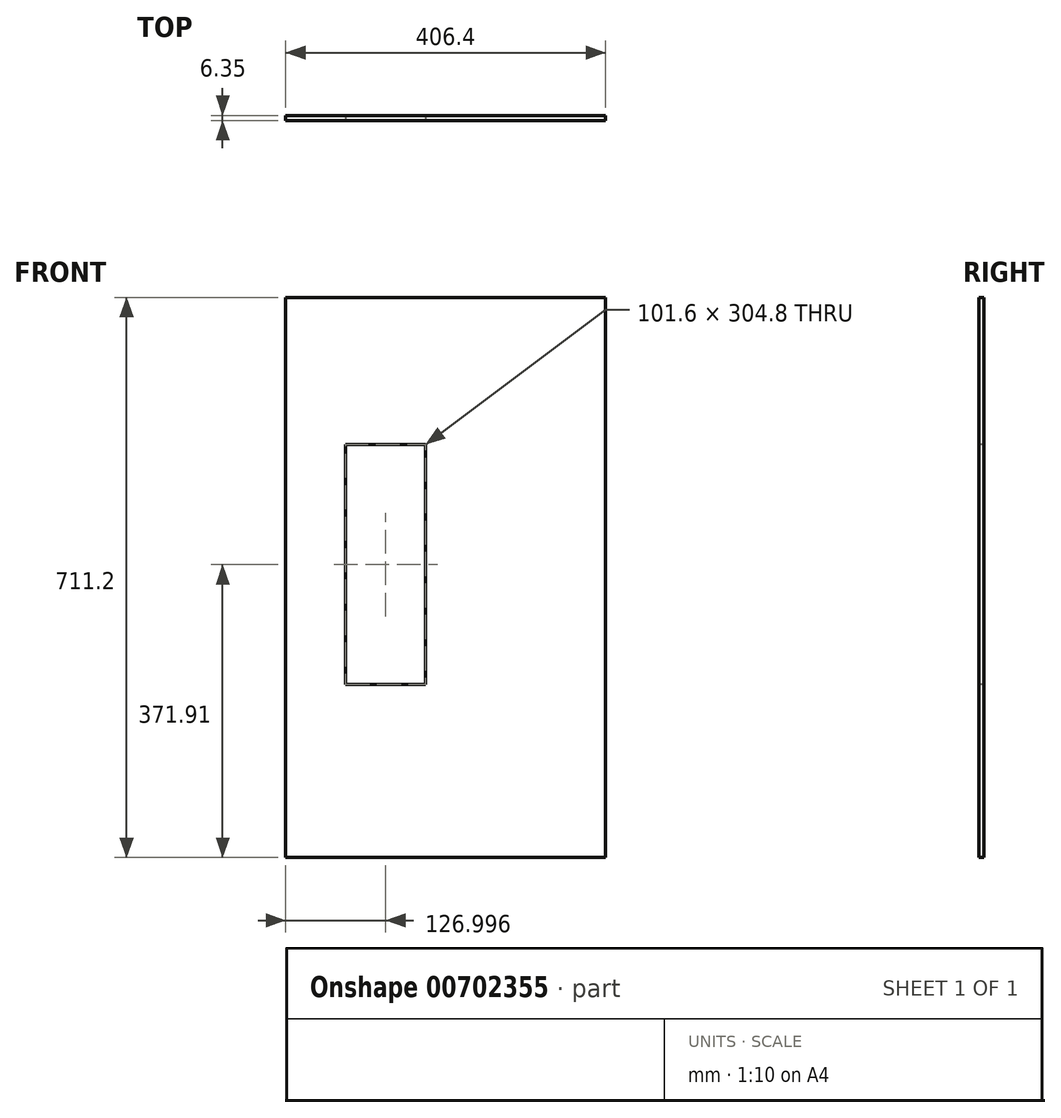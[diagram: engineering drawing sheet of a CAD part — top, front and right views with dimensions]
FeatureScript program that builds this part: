
annotation { "Feature Type Name" : "Feature", "Feature Type Description" : "" }
export const myFeature = defineFeature(function(context is Context, id is Id, definition is map)
    precondition{}
    {
        {
            var Q0;
            Q0=qCreatedBy(makeId("Front.planeOp"),FACE);
            var sketch = newSketch(context, id + "F0", { "sketchPlane" : qUnion([Q0])});
            skLineSegment(sketch, "E0.bottom", {"start": v(-192.42, 355.6) * mm, "end": v(213.98, 355.6) * mm});
            skLineSegment(sketch, "E0.top", {"start": v(-192.42, -355.6) * mm, "end": v(213.98, -355.6) * mm});
            skLineSegment(sketch, "E0.left", {"start": v(-192.42, 355.6) * mm, "end": v(-192.42, -355.6) * mm});
            skLineSegment(sketch, "E0.right", {"start": v(213.98, 355.6) * mm, "end": v(213.98, -355.6) * mm});
            skPoint(sketch, "E0.middle", {"position": v(10.78, 0) * mm});
            skSolve(sketch);
        }
        {
            var Q0;
            Q0=makeQuery(id+"F0.imprint","IMPRINT",FACE,{"disambiguationData":[TD([[makeQuery(id+"F0.imprint","IMPRINT",EDGE,{"derivedFrom":sQuery(id+"F0.wireOp",EDGE,"E0.bottom")}),-1.0]])]});
            extrude(context, id + "F1", {"entities" : qUnion([Q0]), "endBound" : BoundingType.SYMMETRIC, "depth" : 6.35 * mm, "offsetDistance" : 25.4 * mm});
        }
        {
            var Q0;
            Q0=makeQuery(id+"F1.opExtrude","CAP_FACE",FACE,{"disambiguationData":[OSD([sQuery(id+"F0.wireOp",EDGE,"E0.bottom"),sQuery(id+"F0.wireOp",EDGE,"E0.top"),sQuery(id+"F0.wireOp",EDGE,"E0.left"),sQuery(id+"F0.wireOp",EDGE,"E0.right")])],"isStart":false});
            var sketch = newSketch(context, id + "F2", { "sketchPlane" : qUnion([Q0])});
            skLineSegment(sketch, "E1.bottom", {"start": v(-116.22, 168.71) * mm, "end": v(-14.62, 168.71) * mm});
            skLineSegment(sketch, "E1.top", {"start": v(-116.22, -136.09) * mm, "end": v(-14.62, -136.09) * mm});
            skLineSegment(sketch, "E1.left", {"start": v(-116.22, 168.71) * mm, "end": v(-116.22, -136.09) * mm});
            skLineSegment(sketch, "E1.right", {"start": v(-14.62, 168.71) * mm, "end": v(-14.62, -136.09) * mm});
            skSolve(sketch);
        }
        {
            var Q0;
            Q0=makeQuery(id+"F2.imprint","IMPRINT",FACE,{"disambiguationData":[TD([[makeQuery(id+"F2.imprint","IMPRINT",EDGE,{"derivedFrom":sQuery(id+"F2.wireOp",EDGE,"E1.bottom")}),-1.0]])]});
            extrude(context, id + "F3", {"entities" : qUnion([Q0]), "operationType" : NewBodyOperationType.REMOVE, "endBound" : BoundingType.THROUGH_ALL, "oppositeDirection" : true, "depth" : 25.4 * mm, "offsetDistance" : 25.4 * mm});
        }
    });
